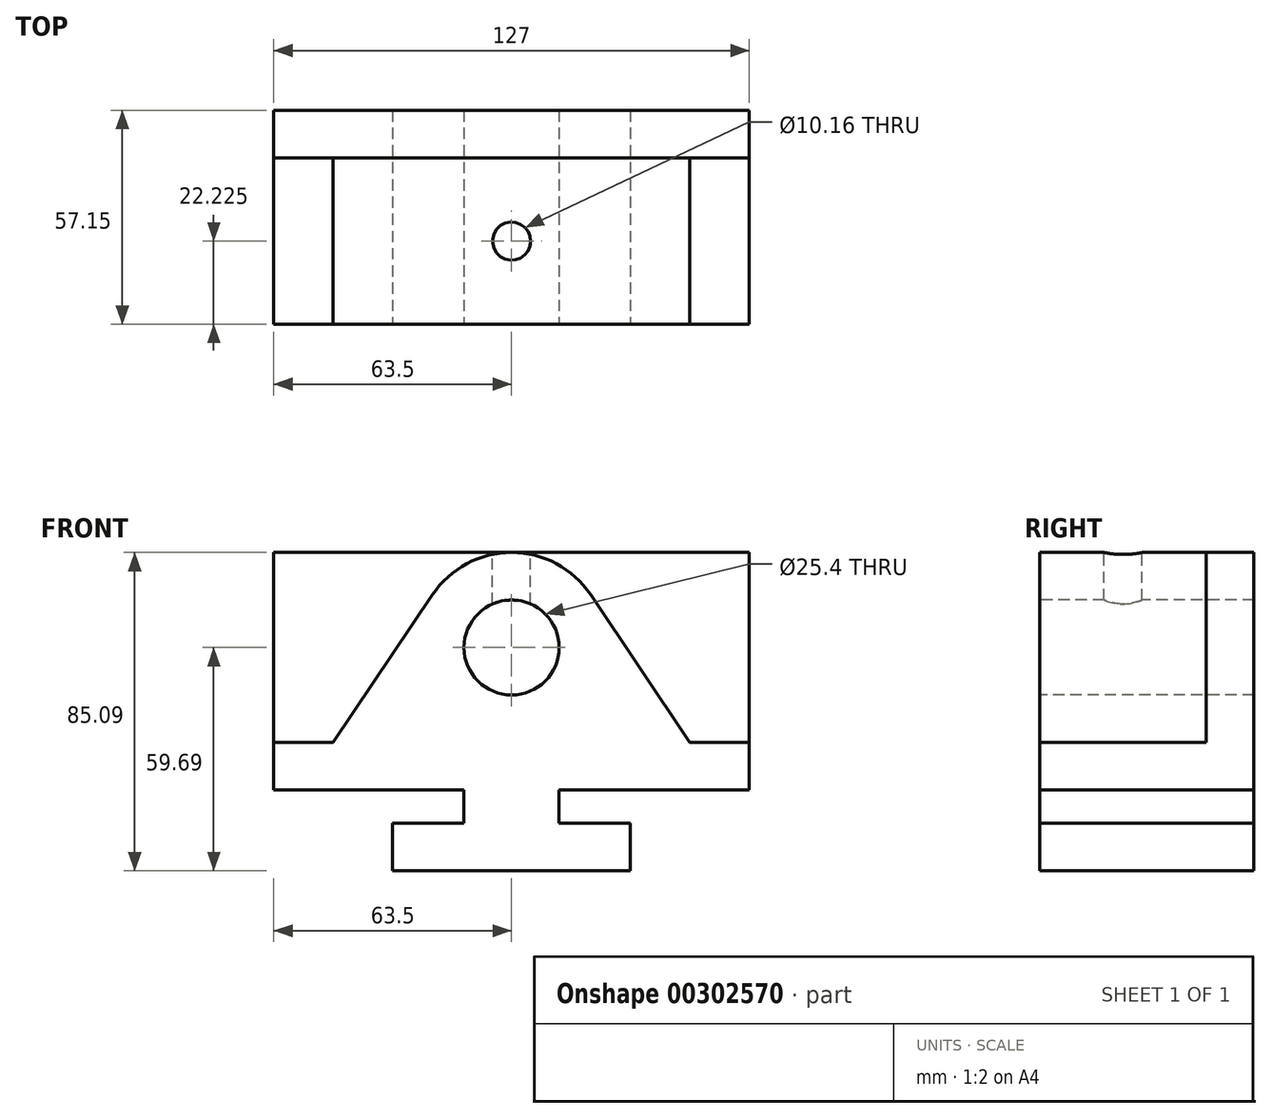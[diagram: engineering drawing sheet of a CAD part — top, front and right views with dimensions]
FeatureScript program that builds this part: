
annotation { "Feature Type Name" : "Feature", "Feature Type Description" : "" }
export const myFeature = defineFeature(function(context is Context, id is Id, definition is map)
    precondition{}
    {
        {
            var Q0;
            Q0=qCreatedBy(makeId("Front.planeOp"),FACE);
            var sketch = newSketch(context, id + "F0", { "sketchPlane" : qUnion([Q0])});
            skLineSegment(sketch, "E0.bottom", {"start": v(-63.5, 0) * mm, "end": v(63.5, 0) * mm, "construction": true});
            skLineSegment(sketch, "E0.top", {"start": v(-63.5, 63.5) * mm, "end": v(63.5, 63.5) * mm, "construction": true});
            skLineSegment(sketch, "E0.left", {"start": v(-63.5, 0) * mm, "end": v(-63.5, 63.5) * mm, "construction": true});
            skLineSegment(sketch, "E0.right", {"start": v(63.5, 0) * mm, "end": v(63.5, 63.5) * mm, "construction": true});
            skLineSegment(sketch, "E1", {"start": v(0, 63.5) * mm, "end": v(0, -21.59) * mm, "construction": true});
            skLineSegment(sketch, "E2", {"start": v(-31.75, -21.59) * mm, "end": v(31.75, -21.59) * mm});
            skLineSegment(sketch, "E3", {"start": v(31.75, -21.59) * mm, "end": v(31.75, -8.89) * mm});
            skLineSegment(sketch, "E4", {"start": v(31.75, -8.89) * mm, "end": v(12.7, -8.89) * mm});
            skLineSegment(sketch, "E5", {"start": v(12.7, -8.89) * mm, "end": v(12.7, 0) * mm});
            skLineSegment(sketch, "E6", {"start": v(12.7, 0) * mm, "end": v(63.5, 0) * mm});
            skLineSegment(sketch, "E7", {"start": v(63.5, 63.5) * mm, "end": v(63.5, 0) * mm});
            skLineSegment(sketch, "E8", {"start": v(63.5, 63.5) * mm, "end": v(0, 63.5) * mm});
            skLineSegment(sketch, "E9", {"start": v(63.5, 12.7) * mm, "end": v(47.63, 12.7) * mm});
            skCircle(sketch, "E10", {"center": v(0, 38.1) * mm, "radius": 12.7 * mm});
            skLineSegment(sketch, "E11", {"start": v(47.63, 12.7) * mm, "end": v(21.1, 52.25) * mm});
            skLineSegment(sketch, "E12.MirrorCS", {"start": v(-47.63, 12.7) * mm, "end": v(-21.1, 52.25) * mm});
            skLineSegment(sketch, "E13.MirrorCS", {"start": v(-63.5, 63.5) * mm, "end": v(0, 63.5) * mm});
            skLineSegment(sketch, "E14.MirrorCS", {"start": v(-63.5, 63.5) * mm, "end": v(-63.5, 0) * mm});
            skLineSegment(sketch, "E15.MirrorCS", {"start": v(-12.7, 0) * mm, "end": v(-63.5, 0) * mm});
            skLineSegment(sketch, "E16.MirrorCS", {"start": v(-63.5, 12.7) * mm, "end": v(-47.63, 12.7) * mm});
            skLineSegment(sketch, "E17.MirrorCS", {"start": v(-12.7, -8.89) * mm, "end": v(-12.7, 0) * mm});
            skLineSegment(sketch, "E18.MirrorCS", {"start": v(-31.75, -8.9) * mm, "end": v(-12.7, -8.89) * mm});
            skLineSegment(sketch, "E19.MirrorCS", {"start": v(-31.75, -21.6) * mm, "end": v(-31.75, -8.9) * mm});
            skArc(sketch, "E20", {"start": v(21.1, 52.25) * mm, "mid": v(0, 63.5) * mm, "end": v(-21.1, 52.25) * mm});
            skSolve(sketch);
        }
        {
            var Q0;
            Q0 = qSketchRegion(id + "F0", true);
            extrude(context, id + "F1", {"entities" : qUnion([Q0]), "oppositeDirection" : true, "depth" : 57.15 * mm});
        }
        {
            var Q0;
            {var subQ3=sQuery(id+"F0.wireOp",EDGE,"E12.MirrorCS");Q0=makeQuery(id+"F0.imprint","IMPRINT",FACE,{"disambiguationData":[TD([[makeQuery(id+"F0.imprint","IMPRINT",EDGE,{"derivedFrom":subQ3}),1.0]])]});}
            var Q1;
            {var subQ1=sQuery(id+"F0.wireOp",EDGE,"E8");Q1=makeQuery(id+"F0.imprint","IMPRINT",FACE,{"disambiguationData":[TD([[makeQuery(id+"F0.imprint","IMPRINT",EDGE,{"derivedFrom":subQ1}),1.0]])]});}
            extrude(context, id + "F2", {"entities" : qUnion([Q0, Q1]), "operationType" : NewBodyOperationType.REMOVE, "oppositeDirection" : true, "depth" : 44.45 * mm});
        }
        {
            var Q0;
            Q0=makeQuery(id+"F1.opExtrude","SWEPT_FACE",FACE,{"disambiguationData":[OSD([sQuery(id+"F0.wireOp",EDGE,"E8"),sQuery(id+"F0.wireOp",EDGE,"E13.MirrorCS")])]});
            var sketch = newSketch(context, id + "F3", { "sketchPlane" : qUnion([Q0])});
            skLineSegment(sketch, "E21", {"start": v(0, 57.15) * mm, "end": v(0, 0) * mm, "construction": true});
            skCircle(sketch, "E22", {"center": v(0, 22.23) * mm, "radius": 5.08 * mm});
            skSolve(sketch);
        }
        {
            var Q0;
            Q0 = qSketchRegion(id + "F3", true);
            extrude(context, id + "F4", {"entities" : qUnion([Q0]), "operationType" : NewBodyOperationType.REMOVE, "endBound" : BoundingType.UP_TO_NEXT, "oppositeDirection" : true, "depth" : 25.4 * mm});
        }
    });
